# Revit family: Sun-Shades_ARUNA_PalmSHIELD
name_source: partatom
category: Generic Models
units: mm (PartAtom-declared; Revit-internal decimal feet)

## family parameters
Always vertical = Yes
Can host rebar = No
Cut with Voids When Loaded = No
Maintain Annotation Orientation = No
Part Type = Normal
Room Calculation Point = No
Round Connector Dimension = Use Diameter
Shared = No
Work Plane-Based = No

## types (14) — shared parameters
CAD Details = https://www.arcat.com
Default Elevation = 0' - 0"
Keynote = 06 87 00
Manufacturer = PalmSHIELD
Product Page URL = https://www.arcat.com
Specification = https://www.arcat.com
URL = https://palmshieldlouvers.com

## per-type parameters (varying)
| type | Finish | Purlin Height | Purlin Width | Purlin offset from column |
| ALUMINUM PURLINS 2" x 3" | PalmSHIELD - Aluminum | 0' - 3" | 0' - 2" | 0' - 1" |
| ALUMINUM PURLINS 1" x 3" | PalmSHIELD - Aluminum | 0' - 3" | 0' - 1" | 0' - 0 1/2" |
| ALUMINUM PURLINS 1" x 4" | PalmSHIELD - Aluminum | 0' - 4" | 0' - 1" | 0' - 0 1/2" |
| ALUMINUM PURLINS 2" x 2" | PalmSHIELD - Aluminum | 0' - 2" | 0' - 2" | 0' - 1" |
| ALUMINUM PURLINS 3" x 3" | PalmSHIELD - Aluminum | 0' - 3" | 0' - 3" | 0' - 1 1/2" |
| ALUMINUM PURLINS 2" x 4" | PalmSHIELD - Aluminum | 0' - 4" | 0' - 2" | 0' - 1" |
| ALUMINUM PURLINS 2" x 5" | PalmSHIELD - Aluminum | 0' - 5" | 0' - 2" | 0' - 1" |
| ALUMINUM PURLINS 2" x 6" | PalmSHIELD - Aluminum | 0' - 6" | 0' - 2" | 0' - 1" |
| ALUMINUM PURLINS 2" x 8" | PalmSHIELD - Aluminum | 0' - 8" | 0' - 2" | 0' - 1" |
| Wood Finished 2" x 4" | PalmSHIELD - Wood | 0' - 4" | 0' - 2" | 0' - 1" |
| Wood Finished 2" x 6" | PalmSHIELD - Wood | 0' - 6" | 0' - 2" | 0' - 1" |
| Wood Finished 2" x 8" | PalmSHIELD - Wood | 0' - 8" | 0' - 2" | 0' - 1" |
| Wood Finished 2" x 10" | PalmSHIELD - Wood | 0' - 10" | 0' - 2" | 0' - 1" |
| Wood Finished 4" x 4" | PalmSHIELD - Wood | 0' - 4" | 0' - 4" | 0' - 2" |

## geometry (parser evidence)
native form markers: Sweep x8
no freeform markers — native parametric forms only
